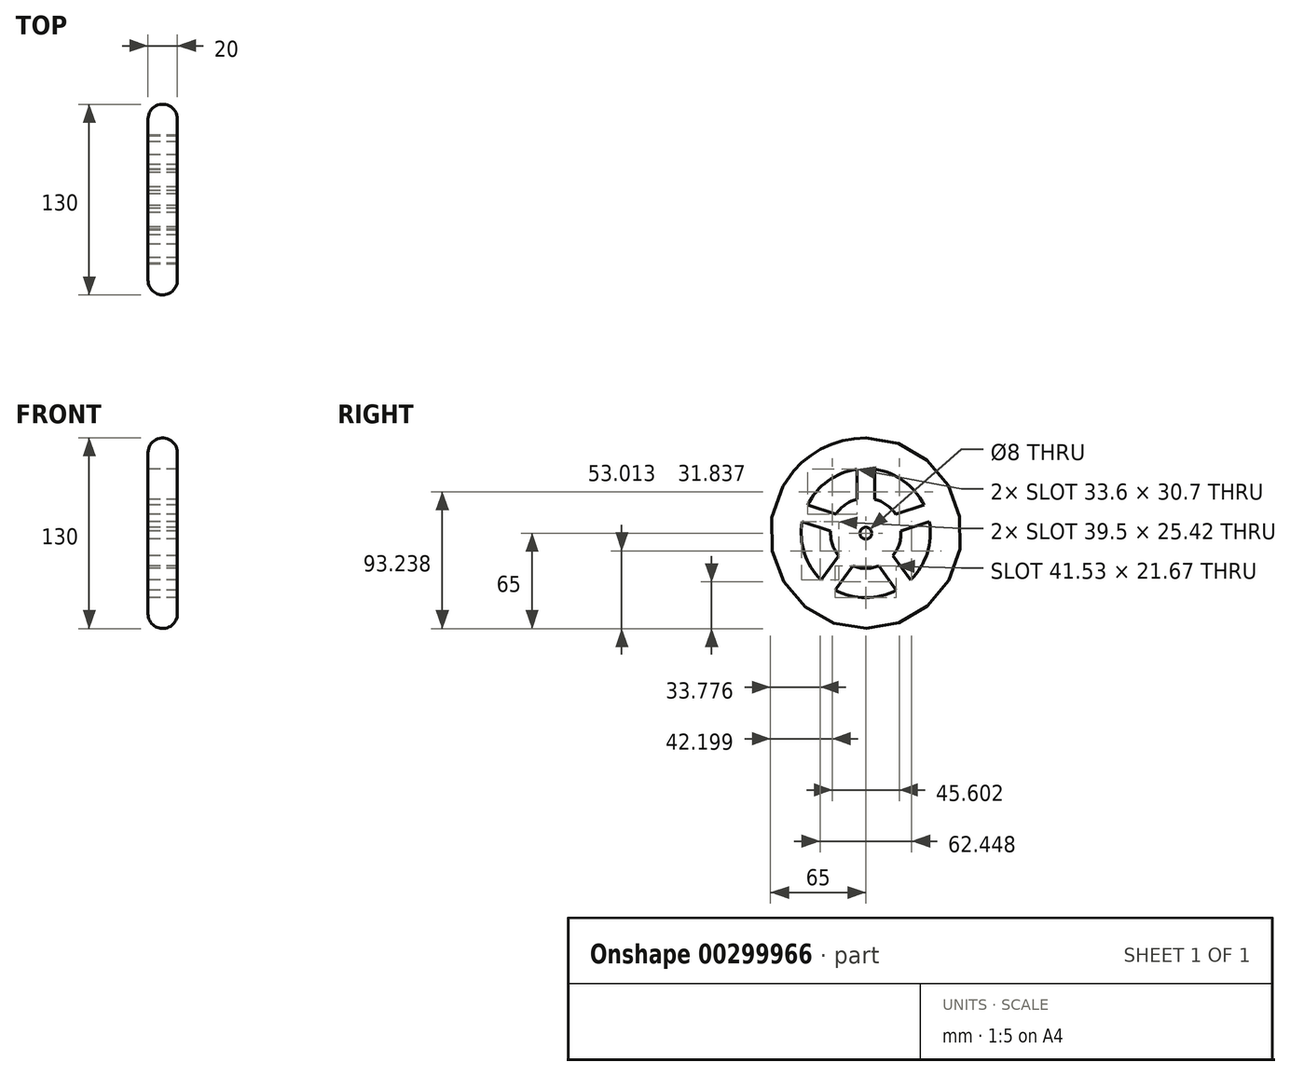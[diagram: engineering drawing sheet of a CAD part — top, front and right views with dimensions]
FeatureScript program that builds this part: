
annotation { "Feature Type Name" : "Feature", "Feature Type Description" : "" }
export const myFeature = defineFeature(function(context is Context, id is Id, definition is map)
    precondition{}
    {
        {
            var Q0;
            Q0=qCreatedBy(makeId("Front.planeOp"),FACE);
            var sketch = newSketch(context, id + "F0", { "sketchPlane" : qUnion([Q0])});
            skLineSegment(sketch, "E0", {"start": v(-145.45, 0) * mm, "end": v(120, 0) * mm});
            skLineSegment(sketch, "E1", {"start": v(-10, 4) * mm, "end": v(10, 4) * mm});
            skLineSegment(sketch, "E2", {"start": v(-10, 4) * mm, "end": v(-10, 59.23) * mm});
            skLineSegment(sketch, "E3", {"start": v(10, 4) * mm, "end": v(10, 59.04) * mm});
            skCircle(sketch, "E4", {"center": v(0, 55) * mm, "radius": 10 * mm});
            skSolve(sketch);
        }
        {
            var Q0;
            Q0 = qSketchRegion(id + "F0", true);
            var Q1;
            Q1=sQuery(id+"F0.wireOp",EDGE,"E0");
            revolve(context, id + "F1", {"entities" : qUnion([Q0]), "axis" : qUnion([Q1]), "revolveType" : RevolveType.FULL});
        }
        {
            var Q0;
            Q0=makeQuery(id+"F1.opRevolve","SWEPT_FACE",FACE,{"disambiguationData":[OSD([sQuery(id+"F0.wireOp",EDGE,"E2")])]});
            var sketch = newSketch(context, id + "F2", { "sketchPlane" : qUnion([Q0])});
            skCircle(sketch, "E5", {"center": v(0, 0) * mm, "radius": 24 * mm});
            skCircle(sketch, "E6", {"center": v(0, 0) * mm, "radius": 44 * mm});
            skLineSegment(sketch, "E7.bottom", {"start": v(-6, 49.38) * mm, "end": v(6, 49.38) * mm});
            skLineSegment(sketch, "E7.top", {"start": v(-6, 18.07) * mm, "end": v(6, 18.07) * mm});
            skLineSegment(sketch, "E7.left", {"start": v(-6, 49.38) * mm, "end": v(-6, 18.07) * mm});
            skLineSegment(sketch, "E7.right", {"start": v(6, 49.38) * mm, "end": v(6, 18.07) * mm});
            skLineSegment(sketch, "E8.1.0", {"start": v(-45.1, 20.96) * mm, "end": v(-15.33, 11.29) * mm});
            skLineSegment(sketch, "E8.1.1", {"start": v(-48.81, 9.55) * mm, "end": v(-45.1, 20.96) * mm});
            skLineSegment(sketch, "E8.1.2", {"start": v(-48.81, 9.55) * mm, "end": v(-19.04, -0.12) * mm});
            skLineSegment(sketch, "E8.1.3", {"start": v(-19.04, -0.12) * mm, "end": v(-15.33, 11.29) * mm});
            skLineSegment(sketch, "E8.2.0", {"start": v(-33.88, -36.42) * mm, "end": v(-15.47, -11.1) * mm});
            skLineSegment(sketch, "E8.2.1", {"start": v(-24.17, -43.47) * mm, "end": v(-33.88, -36.42) * mm});
            skLineSegment(sketch, "E8.2.2", {"start": v(-24.17, -43.47) * mm, "end": v(-5.77, -18.14) * mm});
            skLineSegment(sketch, "E8.2.3", {"start": v(-5.77, -18.14) * mm, "end": v(-15.47, -11.1) * mm});
            skLineSegment(sketch, "E8.3.0", {"start": v(24.17, -43.47) * mm, "end": v(5.77, -18.14) * mm});
            skLineSegment(sketch, "E8.3.1", {"start": v(33.88, -36.42) * mm, "end": v(24.17, -43.47) * mm});
            skLineSegment(sketch, "E8.3.2", {"start": v(33.88, -36.42) * mm, "end": v(15.47, -11.1) * mm});
            skLineSegment(sketch, "E8.3.3", {"start": v(15.47, -11.1) * mm, "end": v(5.77, -18.14) * mm});
            skLineSegment(sketch, "E8.4.0", {"start": v(48.81, 9.55) * mm, "end": v(19.04, -0.12) * mm});
            skLineSegment(sketch, "E8.4.1", {"start": v(45.1, 20.96) * mm, "end": v(48.81, 9.55) * mm});
            skLineSegment(sketch, "E8.4.2", {"start": v(45.1, 20.96) * mm, "end": v(15.33, 11.29) * mm});
            skLineSegment(sketch, "E8.4.3", {"start": v(15.33, 11.29) * mm, "end": v(19.04, -0.12) * mm});
            skSolve(sketch);
        }
        {
            var Q0;
            {var subQ0=sQuery(id+"F2.wireOp",EDGE,"E8.1.2");var subQ1=sQuery(id+"F2.wireOp",EDGE,"E5");var subQ2=makeQuery(id+"F2.imprint","INTERSECT",VERTEX,{"derivedFrom":[subQ1,subQ0]});Q0=makeQuery(id+"F2.imprint","IMPRINT",FACE,{"disambiguationData":[TD([[makeQuery(id+"F2.imprint","IMPRINT",EDGE,{"disambiguationData":[TD([[subQ2,-1.0]])],"derivedFrom":subQ1}),-1.0]])]});}
            var Q1;
            {var subQ0=sQuery(id+"F2.wireOp",EDGE,"E8.2.2");var subQ1=sQuery(id+"F2.wireOp",EDGE,"E5");var subQ2=makeQuery(id+"F2.imprint","INTERSECT",VERTEX,{"derivedFrom":[subQ1,subQ0]});Q1=makeQuery(id+"F2.imprint","IMPRINT",FACE,{"disambiguationData":[TD([[makeQuery(id+"F2.imprint","IMPRINT",EDGE,{"disambiguationData":[TD([[subQ2,-1.0]])],"derivedFrom":subQ1}),-1.0]])]});}
            var Q2;
            {var subQ0=sQuery(id+"F2.wireOp",EDGE,"E8.4.0");var subQ1=sQuery(id+"F2.wireOp",EDGE,"E5");var subQ2=makeQuery(id+"F2.imprint","INTERSECT",VERTEX,{"derivedFrom":[subQ1,subQ0]});Q2=makeQuery(id+"F2.imprint","IMPRINT",FACE,{"disambiguationData":[TD([[makeQuery(id+"F2.imprint","IMPRINT",EDGE,{"disambiguationData":[TD([[subQ2,1.0]])],"derivedFrom":subQ1}),-1.0]])]});}
            var Q3;
            {var subQ0=sQuery(id+"F2.wireOp",EDGE,"E7.left");var subQ1=sQuery(id+"F2.wireOp",EDGE,"E5");var subQ2=makeQuery(id+"F2.imprint","INTERSECT",VERTEX,{"derivedFrom":[subQ1,subQ0]});Q3=makeQuery(id+"F2.imprint","IMPRINT",FACE,{"disambiguationData":[TD([[makeQuery(id+"F2.imprint","IMPRINT",EDGE,{"disambiguationData":[TD([[subQ2,-1.0]])],"derivedFrom":subQ1}),-1.0]])]});}
            var Q4;
            {var subQ0=sQuery(id+"F2.wireOp",EDGE,"E8.4.2");var subQ1=sQuery(id+"F2.wireOp",EDGE,"E5");var subQ2=makeQuery(id+"F2.imprint","INTERSECT",VERTEX,{"derivedFrom":[subQ1,subQ0]});Q4=makeQuery(id+"F2.imprint","IMPRINT",FACE,{"disambiguationData":[TD([[makeQuery(id+"F2.imprint","IMPRINT",EDGE,{"disambiguationData":[TD([[subQ2,-1.0]])],"derivedFrom":subQ1}),-1.0]])]});}
            extrude(context, id + "F3", {"entities" : qUnion([Q0, Q1, Q2, Q3, Q4]), "operationType" : NewBodyOperationType.REMOVE, "oppositeDirection" : true, "depth" : 25 * mm});
        }
    });
